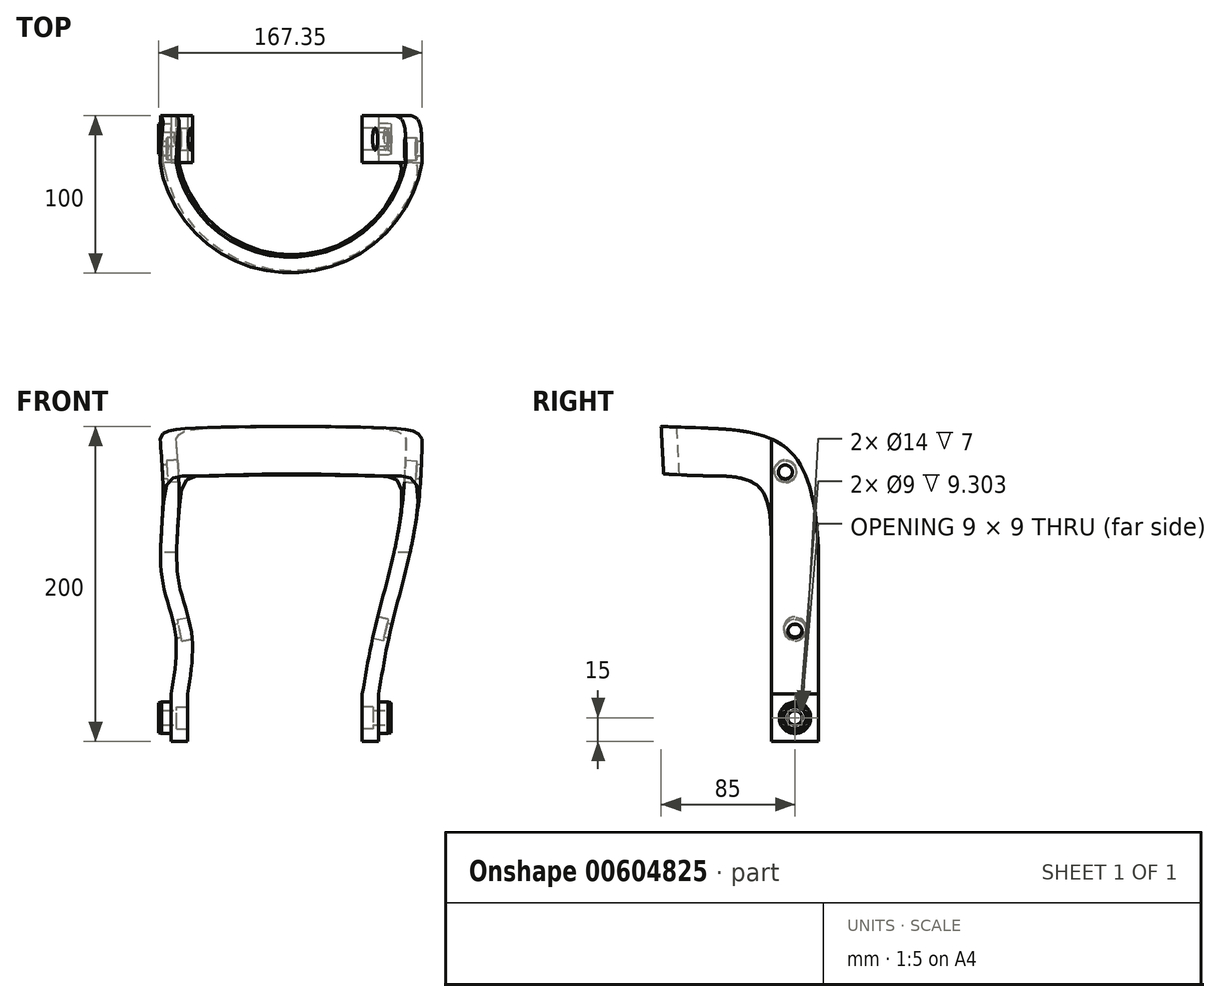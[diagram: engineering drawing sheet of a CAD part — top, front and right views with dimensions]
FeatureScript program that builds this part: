
annotation { "Feature Type Name" : "Feature", "Feature Type Description" : "" }
export const myFeature = defineFeature(function(context is Context, id is Id, definition is map)
    precondition{}
    {
        {
            var Q0;
            Q0=qCreatedBy(makeId("Top.planeOp"),FACE);
            var sketch = newSketch(context, id + "F0", { "sketchPlane" : qUnion([Q0])});
            skLineSegment(sketch, "E0", {"start": v(-55.5, 15) * mm, "end": v(-55.5, -15) * mm});
            skLineSegment(sketch, "E1", {"start": v(55.5, 15) * mm, "end": v(55.5, -15) * mm});
            skPoint(sketch, "E2", {"position": v(-55.5, 0) * mm});
            skPoint(sketch, "E3", {"position": v(55.5, 0) * mm});
            skLineSegment(sketch, "E4", {"start": v(-55.5, 15) * mm, "end": v(-65.81, 15) * mm});
            skLineSegment(sketch, "E5", {"start": v(-65.81, 15) * mm, "end": v(-65.81, -15) * mm});
            skLineSegment(sketch, "E6", {"start": v(55.5, 15) * mm, "end": v(65.81, 15) * mm});
            skLineSegment(sketch, "E7", {"start": v(65.81, 15) * mm, "end": v(65.81, -15) * mm});
            skLineSegment(sketch, "E8", {"start": v(-65.81, -15) * mm, "end": v(-55.5, -15) * mm});
            skLineSegment(sketch, "E9", {"start": v(55.5, -15) * mm, "end": v(65.81, -15) * mm});
            skSolve(sketch);
        }
        {
            var Q0;
            Q0=qCreatedBy(makeId("Top.planeOp"),FACE);
            cPlane(context, id + "F1", {"entities" : qUnion([Q0]), "cplaneType" : CPlaneType.OFFSET, "offset" : 30 * mm, "width" : 150 * mm, "height" : 150 * mm});
        }
        {
            var Q0;
            Q0=qCreatedBy(id+"F1.planeOp",FACE);
            var sketch = newSketch(context, id + "F2", { "sketchPlane" : qUnion([Q0])});
            skArc(sketch, "E10", {"start": v(-55.5, -15) * mm, "mid": v(0, -57.5) * mm, "end": v(55.5, -15) * mm});
            skArc(sketch, "E11", {"start": v(-65.81, -15) * mm, "mid": v(0, -67.5) * mm, "end": v(65.81, -15) * mm});
            skLineSegment(sketch, "E12", {"start": v(-55.5, 15) * mm, "end": v(-55.5, -15) * mm});
            skLineSegment(sketch, "E13", {"start": v(55.5, 15) * mm, "end": v(55.5, -15) * mm});
            skPoint(sketch, "E14", {"position": v(-55.5, 0) * mm});
            skPoint(sketch, "E15", {"position": v(55.5, 0) * mm});
            skLineSegment(sketch, "E16", {"start": v(-55.5, 15) * mm, "end": v(-65.81, 15) * mm});
            skLineSegment(sketch, "E17", {"start": v(-65.81, 15) * mm, "end": v(-65.81, -15) * mm});
            skLineSegment(sketch, "E18", {"start": v(55.5, 15) * mm, "end": v(65.81, 15) * mm});
            skLineSegment(sketch, "E19", {"start": v(65.81, 15) * mm, "end": v(65.81, -15) * mm});
            skSolve(sketch);
        }
        {
            var Q0;
            Q0=qCreatedBy(makeId("Top.planeOp"),FACE);
            cPlane(context, id + "F3", {"entities" : qUnion([Q0]), "cplaneType" : CPlaneType.OFFSET, "offset" : 70 * mm, "width" : 150 * mm, "height" : 150 * mm});
        }
        {
            var Q0;
            Q0=qCreatedBy(id+"F3.planeOp",FACE);
            var sketch = newSketch(context, id + "F4", { "sketchPlane" : qUnion([Q0])});
            skPoint(sketch, "E20", {"position": v(5, 0) * mm});
            skPoint(sketch, "E21.center.orphan", {"position": v(0, 0) * mm});
            skArc(sketch, "E22", {"start": v(-53.1, -15) * mm, "mid": v(5, -60) * mm, "end": v(63.1, -15) * mm});
            skArc(sketch, "E23", {"start": v(-63.37, -15) * mm, "mid": v(5, -70) * mm, "end": v(73.37, -15) * mm});
            skLineSegment(sketch, "E24", {"start": v(-53.1, 15) * mm, "end": v(-53.1, -15) * mm});
            skLineSegment(sketch, "E25", {"start": v(63.1, 15) * mm, "end": v(63.1, -15) * mm});
            skPoint(sketch, "E26", {"position": v(-53.1, 0) * mm});
            skLineSegment(sketch, "E27", {"start": v(-53.1, 15) * mm, "end": v(-63.37, 15) * mm});
            skLineSegment(sketch, "E28", {"start": v(-63.37, 15) * mm, "end": v(-63.37, -15) * mm});
            skLineSegment(sketch, "E29", {"start": v(63.1, 15) * mm, "end": v(73.37, 15) * mm});
            skLineSegment(sketch, "E30", {"start": v(73.37, 15) * mm, "end": v(73.37, -15) * mm});
            skSolve(sketch);
        }
        {
            var Q0;
            Q0=qCreatedBy(makeId("Top.planeOp"),FACE);
            cPlane(context, id + "F5", {"entities" : qUnion([Q0]), "cplaneType" : CPlaneType.OFFSET, "offset" : 100 * mm, "width" : 150 * mm, "height" : 150 * mm});
        }
        {
            var Q0;
            Q0=qCreatedBy(id+"F5.planeOp",FACE);
            var sketch = newSketch(context, id + "F6", { "sketchPlane" : qUnion([Q0])});
            skPoint(sketch, "E31", {"position": v(5, 0) * mm});
            skArc(sketch, "E32", {"start": v(-60.81, -15) * mm, "mid": v(5, -67.5) * mm, "end": v(70.81, -15) * mm});
            skArc(sketch, "E33", {"start": v(-71.03, -15) * mm, "mid": v(5, -77.5) * mm, "end": v(81.03, -15) * mm});
            skLineSegment(sketch, "E34", {"start": v(-60.81, 15) * mm, "end": v(-60.81, -15) * mm});
            skLineSegment(sketch, "E35", {"start": v(70.81, 15) * mm, "end": v(70.81, -15) * mm});
            skLineSegment(sketch, "E36", {"start": v(-60.81, 15) * mm, "end": v(-71.03, 15) * mm});
            skLineSegment(sketch, "E37", {"start": v(-71.03, 15) * mm, "end": v(-71.03, -15) * mm});
            skLineSegment(sketch, "E38", {"start": v(70.81, 15) * mm, "end": v(81.03, 15) * mm});
            skLineSegment(sketch, "E39", {"start": v(81.03, 15) * mm, "end": v(81.03, -15) * mm});
            skSolve(sketch);
        }
        {
            var Q0;
            Q0=qCreatedBy(makeId("Top.planeOp"),FACE);
            cPlane(context, id + "F7", {"entities" : qUnion([Q0]), "cplaneType" : CPlaneType.OFFSET, "offset" : 150 * mm, "width" : 150 * mm, "height" : 150 * mm});
        }
        {
            var Q0;
            Q0=qCreatedBy(id+"F7.planeOp",FACE);
            var sketch = newSketch(context, id + "F8", { "sketchPlane" : qUnion([Q0])});
            skPoint(sketch, "E40", {"position": v(10, 0) * mm});
            skArc(sketch, "E41", {"start": v(-60.93, -15) * mm, "mid": v(10, -72.5) * mm, "end": v(80.93, -15) * mm});
            skArc(sketch, "E42", {"start": v(-71.12, -15) * mm, "mid": v(10, -82.5) * mm, "end": v(91.12, -15) * mm});
            skLineSegment(sketch, "E43", {"start": v(-60.93, 15) * mm, "end": v(-60.93, -15) * mm});
            skLineSegment(sketch, "E44", {"start": v(80.93, -15) * mm, "end": v(80.93, 15) * mm});
            skPoint(sketch, "E45", {"position": v(-60.93, 0) * mm});
            skPoint(sketch, "E46", {"position": v(80.93, 0) * mm});
            skLineSegment(sketch, "E47", {"start": v(-60.93, 15) * mm, "end": v(-71.12, 15) * mm});
            skLineSegment(sketch, "E48", {"start": v(-71.12, 15) * mm, "end": v(-71.12, -15) * mm});
            skLineSegment(sketch, "E49", {"start": v(80.93, 15) * mm, "end": v(91.12, 15) * mm});
            skLineSegment(sketch, "E50", {"start": v(91.12, 15) * mm, "end": v(91.12, -15) * mm});
            skSolve(sketch);
        }
        {
            var Q0;
            Q0=qCreatedBy(makeId("Top.planeOp"),FACE);
            cPlane(context, id + "F9", {"entities" : qUnion([Q0]), "cplaneType" : CPlaneType.OFFSET, "offset" : 200 * mm, "width" : 150 * mm, "height" : 150 * mm});
        }
        {
            var Q0;
            Q0=qCreatedBy(id+"F9.planeOp",FACE);
            var sketch = newSketch(context, id + "F10", { "sketchPlane" : qUnion([Q0])});
            skPoint(sketch, "E51", {"position": v(10, 0) * mm});
            skArc(sketch, "E52", {"start": v(-63.48, -15) * mm, "mid": v(10, -75) * mm, "end": v(83.48, -15) * mm});
            skArc(sketch, "E53", {"start": v(-73.67, -15) * mm, "mid": v(10, -85) * mm, "end": v(93.67, -15) * mm});
            skLineSegment(sketch, "E54", {"start": v(-63.48, 15) * mm, "end": v(-63.48, -15) * mm});
            skLineSegment(sketch, "E55", {"start": v(83.48, 15) * mm, "end": v(83.48, -15) * mm});
            skLineSegment(sketch, "E56", {"start": v(-63.48, 15) * mm, "end": v(-73.67, 15) * mm});
            skLineSegment(sketch, "E57", {"start": v(-73.67, 15) * mm, "end": v(-73.67, -15) * mm});
            skLineSegment(sketch, "E58", {"start": v(83.48, 15) * mm, "end": v(93.67, 15) * mm});
            skLineSegment(sketch, "E59", {"start": v(93.67, 15) * mm, "end": v(93.67, -15) * mm});
            skSolve(sketch);
        }
        {
            var Q0;
            Q0=qSketchRegion(id+"F2",true);
            var Q1;
            Q1=qSketchRegion(id+"F4",true);
            var Q2;
            Q2=qSketchRegion(id+"F6",true);
            var Q3;
            Q3=qSketchRegion(id+"F8",true);
            var Q4;
            Q4=qSketchRegion(id+"F10",true);
            loft(context, id + "F11", {"sheetProfilesArray" : [{ "sheetProfileEntities" : qUnion([Q0]) }, { "sheetProfileEntities" : qUnion([Q1]) }, { "sheetProfileEntities" : qUnion([Q2]) }, { "sheetProfileEntities" : qUnion([Q3]) }, { "sheetProfileEntities" : qUnion([Q4]) }]});
        }
        {
            var Q0;
            Q0=qCreatedBy(makeId("Right.planeOp"),FACE);
            cPlane(context, id + "F12", {"entities" : qUnion([Q0]), "cplaneType" : CPlaneType.OFFSET, "offset" : 77 * mm, "oppositeDirection" : true, "width" : 150 * mm, "height" : 150 * mm});
        }
        {
            var Q0;
            Q0=qCreatedBy(id+"F12.planeOp",FACE);
            var sketch = newSketch(context, id + "F13", { "sketchPlane" : qUnion([Q0])});
            skPoint(sketch, "E60", {"position": v(-85, 200) * mm});
            skLineSegment(sketch, "E61", {"start": v(-85, 200) * mm, "end": v(-85, 170) * mm});
            skPoint(sketch, "E62", {"position": v(15, 200) * mm});
            skLineSegment(sketch, "E63", {"start": v(15, 200) * mm, "end": v(15, 120) * mm});
            skPoint(sketch, "E64", {"position": v(15, 0) * mm});
            skPoint(sketch, "E65", {"position": v(-15, 0) * mm});
            skPoint(sketch, "E66", {"position": v(-15, 200) * mm});
            skFitSpline(sketch, "E67", {"points": [v(-85, 200) * mm, v(15, 120) * mm], "startDerivative": vector(199.24, -8.69) * mm, "endDerivative": vector(9.95, -251.27) * mm});
            skPoint(sketch, "E68", {"position": v(-56.51, 168.7) * mm});
            skPoint(sketch, "E69", {"position": v(-23.21, 161.98) * mm});
            skPoint(sketch, "E70", {"position": v(-50.86, 198.7) * mm});
            skPoint(sketch, "E71", {"position": v(-4.39, 185.34) * mm});
            skPoint(sketch, "E72", {"position": v(-15, 120) * mm});
            skFitSpline(sketch, "E73", {"points": [v(-15, 120) * mm, v(-23.21, 161.98) * mm, v(-56.51, 168.7) * mm, v(-85, 170) * mm], "startDerivative": vector(0.5, 138.75) * mm, "endDerivative": vector(-88.02, 5.85) * mm});
            skLineSegment(sketch, "E74", {"start": v(-15, 120) * mm, "end": v(-15, 0) * mm});
            skLineSegment(sketch, "E75", {"start": v(15, 0) * mm, "end": v(15, 120) * mm});
            skLineSegment(sketch, "E76", {"start": v(-85, 200) * mm, "end": v(15, 200) * mm});
            skLineSegment(sketch, "E77", {"start": v(-85, 170) * mm, "end": v(-82.46, 0) * mm});
            skLineSegment(sketch, "E78", {"start": v(-82.46, 0) * mm, "end": v(-15, 0) * mm});
            skLineSegment(sketch, "E79", {"start": v(-85, 170) * mm, "end": v(-85, 200) * mm});
            skSolve(sketch);
        }
        {
            var Q0;
            Q0=qSketchRegion(id+"F13",true);
            extrude(context, id + "F14", {"entities" : qUnion([Q0]), "operationType" : NewBodyOperationType.REMOVE, "depth" : 300 * mm, "offsetDistance" : 25 * mm});
        }
        {
            var Q0;
            Q0=qCreatedBy(id+"F12.planeOp",FACE);
            var sketch = newSketch(context, id + "F15", { "sketchPlane" : qUnion([Q0])});
            skPoint(sketch, "E80", {"position": v(-8.62, 171.05) * mm});
            skLineSegment(sketch, "E81.bottom", {"start": v(-11.12, 161.05) * mm, "end": v(-6.12, 161.05) * mm});
            skLineSegment(sketch, "E81.top", {"start": v(-11.12, 181.05) * mm, "end": v(-6.12, 181.05) * mm});
            skLineSegment(sketch, "E81.left", {"start": v(-11.12, 161.05) * mm, "end": v(-11.12, 181.05) * mm});
            skLineSegment(sketch, "E81.right", {"start": v(-6.12, 161.05) * mm, "end": v(-6.12, 181.05) * mm});
            skSolve(sketch);
        }
        {
            var Q0;
            Q0=qSketchRegion(id+"F0",true);
            extrude(context, id + "F16", {"entities" : qUnion([Q0]), "operationType" : NewBodyOperationType.ADD, "depth" : 30 * mm, "offsetDistance" : 25 * mm});
        }
        {
            var Q0;
            Q0=makeQuery(id+"F16.opExtrude","SWEPT_FACE",FACE,{"disambiguationData":[OSD([sQuery(id+"F0.wireOp",EDGE,"E7")])]});
            var sketch = newSketch(context, id + "F17", { "sketchPlane" : qUnion([Q0])});
            skPoint(sketch, "E82", {"position": v(-15, 30) * mm});
            skPoint(sketch, "E83", {"position": v(-15, 0) * mm});
            skPoint(sketch, "E84", {"position": v(0, 15) * mm});
            skCircle(sketch, "E85", {"center": v(0, 15) * mm, "radius": 10 * mm});
            skSolve(sketch);
        }
        {
            var Q0;
            Q0=qSketchRegion(id+"F17",true);
            extrude(context, id + "F18", {"entities" : qUnion([Q0]), "operationType" : NewBodyOperationType.ADD, "depth" : 6 * mm, "offsetDistance" : 25 * mm});
        }
        {
            var Q0;
            Q0=makeQuery(id+"F18.opExtrude","CAP_FACE",FACE,{"disambiguationData":[OSD([sQuery(id+"F17.wireOp",EDGE,"E85")])],"isStart":false});
            cPlane(context, id + "F19", {"entities" : qUnion([Q0]), "cplaneType" : CPlaneType.OFFSET, "offset" : 0 * mm, "width" : 150 * mm, "height" : 150 * mm});
        }
        {
            var Q0;
            Q0=makeQuery(id+"F16.opExtrude","SWEPT_FACE",FACE,{"disambiguationData":[OSD([sQuery(id+"F0.wireOp",EDGE,"E1")])]});
            cPlane(context, id + "F20", {"entities" : qUnion([Q0]), "cplaneType" : CPlaneType.OFFSET, "offset" : 0 * mm, "width" : 150 * mm, "height" : 150 * mm});
        }
        {
            var Q0;
            Q0=qCreatedBy(id+"F20.planeOp",FACE);
            var sketch = newSketch(context, id + "F21", { "sketchPlane" : qUnion([Q0])});
            skPoint(sketch, "E86", {"position": v(0, 0) * mm});
            skPoint(sketch, "E87", {"position": v(0, 15) * mm});
            skCircle(sketch, "E88", {"center": v(0, 15) * mm, "radius": 7 * mm});
            skSolve(sketch);
        }
        {
            var Q0;
            Q0=qSketchRegion(id+"F21",true);
            extrude(context, id + "F22", {"entities" : qUnion([Q0]), "operationType" : NewBodyOperationType.REMOVE, "oppositeDirection" : true, "depth" : 7 * mm, "offsetDistance" : 25 * mm});
        }
        {
            var Q0;
            Q0=makeQuery(id+"F16.opExtrude","SWEPT_FACE",FACE,{"disambiguationData":[OSD([sQuery(id+"F0.wireOp",EDGE,"E5")])]});
            cPlane(context, id + "F23", {"entities" : qUnion([Q0]), "cplaneType" : CPlaneType.OFFSET, "offset" : 0 * mm, "width" : 150 * mm, "height" : 150 * mm});
        }
        {
            var Q0;
            Q0=qCreatedBy(id+"F23.planeOp",FACE);
            var sketch = newSketch(context, id + "F24", { "sketchPlane" : qUnion([Q0])});
            skPoint(sketch, "E89", {"position": v(0, 15) * mm});
            skCircle(sketch, "E90", {"center": v(0, 15) * mm, "radius": 10 * mm});
            skSolve(sketch);
        }
        {
            var Q0;
            Q0=qSketchRegion(id+"F24",true);
            extrude(context, id + "F25", {"entities" : qUnion([Q0]), "operationType" : NewBodyOperationType.ADD, "depth" : 6 * mm, "offsetDistance" : 25 * mm});
        }
        {
            var Q0;
            Q0=makeQuery(id+"F25.opExtrude","CAP_FACE",FACE,{"disambiguationData":[OSD([sQuery(id+"F24.wireOp",EDGE,"E90")])],"isStart":false});
            cPlane(context, id + "F26", {"entities" : qUnion([Q0]), "cplaneType" : CPlaneType.OFFSET, "offset" : 0 * mm, "width" : 150 * mm, "height" : 150 * mm});
        }
        {
            var Q0;
            Q0=makeQuery(id+"F16.opExtrude","SWEPT_FACE",FACE,{"disambiguationData":[OSD([sQuery(id+"F0.wireOp",EDGE,"E0")])]});
            cPlane(context, id + "F27", {"entities" : qUnion([Q0]), "cplaneType" : CPlaneType.OFFSET, "offset" : 0 * mm, "width" : 150 * mm, "height" : 150 * mm});
        }
        {
            var Q0;
            Q0=qCreatedBy(id+"F27.planeOp",FACE);
            var sketch = newSketch(context, id + "F28", { "sketchPlane" : qUnion([Q0])});
            skPoint(sketch, "E91", {"position": v(0, 0) * mm});
            skPoint(sketch, "E92", {"position": v(0, 15) * mm});
            skCircle(sketch, "E93", {"center": v(0, 15) * mm, "radius": 7 * mm});
            skSolve(sketch);
        }
        {
            var Q0;
            Q0=qSketchRegion(id+"F28",true);
            extrude(context, id + "F29", {"entities" : qUnion([Q0]), "operationType" : NewBodyOperationType.REMOVE, "oppositeDirection" : true, "depth" : 7 * mm, "offsetDistance" : 25 * mm});
        }
        {
            var Q0;
            Q0=makeQuery(id+"F16.opExtrude","CAP_FACE",FACE,{"disambiguationData":[OSD([sQuery(id+"F0.wireOp",EDGE,"E1"),sQuery(id+"F0.wireOp",EDGE,"E6"),sQuery(id+"F0.wireOp",EDGE,"E7"),sQuery(id+"F0.wireOp",EDGE,"E9")])],"isStart":true});
            cPlane(context, id + "F30", {"entities" : qUnion([Q0]), "cplaneType" : CPlaneType.OFFSET, "offset" : 15 * mm, "oppositeDirection" : true, "width" : 150 * mm, "height" : 150 * mm});
        }
        {
            var Q0;
            Q0=qCreatedBy(id+"F30.planeOp",FACE);
            var sketch = newSketch(context, id + "F31", { "sketchPlane" : qUnion([Q0])});
            skPoint(sketch, "E94", {"position": v(60.66, -15) * mm});
            skLineSegment(sketch, "E95", {"start": v(60.66, -15) * mm, "end": v(61.72, -15) * mm, "construction": true});
            skPoint(sketch, "E96", {"position": v(71.81, 4.05) * mm});
            skPoint(sketch, "E97", {"position": v(71.81, -12) * mm});
            skPoint(sketch, "E98", {"position": v(71.81, -15) * mm});
            skPoint(sketch, "E99", {"position": v(41.37, 7.31) * mm});
            skPoint(sketch, "E100", {"position": v(71.81, -13.5) * mm});
            skPoint(sketch, "E101", {"position": v(73.81, -13.5) * mm});
            skPoint(sketch, "E102", {"position": v(73.81, -12.5) * mm});
            skPoint(sketch, "E103", {"position": v(73.81, -14.5) * mm});
            skLineSegment(sketch, "E104", {"start": v(71.81, -12) * mm, "end": v(71.81, -15) * mm});
            skPoint(sketch, "E105", {"position": v(71.81, 0) * mm});
            skPoint(sketch, "E106", {"position": v(71.81, -10) * mm});
            skPoint(sketch, "E107", {"position": v(65.81, -10) * mm});
            skPoint(sketch, "E108", {"position": v(65.81, -7) * mm});
            skPoint(sketch, "E109", {"position": v(65.81, -8.5) * mm});
            skPoint(sketch, "E110", {"position": v(67.81, -8.5) * mm});
            skPoint(sketch, "E111", {"position": v(67.81, -7.5) * mm});
            skPoint(sketch, "E112", {"position": v(67.81, -9.5) * mm});
            skPoint(sketch, "E113", {"position": v(65.81, 0) * mm});
            skLineSegment(sketch, "E114.trimOffspring", {"start": v(71.81, -10) * mm, "end": v(71.81, -16.41) * mm, "construction": true});
            skPoint(sketch, "E115", {"position": v(71.81, -7) * mm});
            skPoint(sketch, "E116", {"position": v(71.81, -8.5) * mm});
            skPoint(sketch, "E117", {"position": v(73.81, -8.5) * mm});
            skPoint(sketch, "E118", {"position": v(73.81, -7.5) * mm});
            skPoint(sketch, "E119", {"position": v(73.81, -9.5) * mm});
            skLineSegment(sketch, "E120", {"start": v(73.81, -7.5) * mm, "end": v(71.81, -7) * mm});
            skLineSegment(sketch, "E121", {"start": v(73.81, -9.5) * mm, "end": v(73.81, -7.5) * mm});
            skLineSegment(sketch, "E122", {"start": v(73.81, -9.5) * mm, "end": v(71.81, -10) * mm});
            skLineSegment(sketch, "E123", {"start": v(71.81, -7) * mm, "end": v(71.81, -10) * mm});
            skLineSegment(sketch, "E124", {"start": v(71.81, 0) * mm, "end": v(73.81, 0) * mm});
            skLineSegment(sketch, "E125", {"start": v(73.81, -8.5) * mm, "end": v(73.81, -9.5) * mm});
            skSolve(sketch);
        }
        {
            var Q0;
            Q0=qSketchRegion(id+"F31",true);
            var Q1;
            Q1=sQuery(id+"F31.wireOp",EDGE,"E124");
            revolve(context, id + "F32", {"operationType" : NewBodyOperationType.ADD, "entities" : qUnion([Q0]), "axis" : qUnion([Q1]), "revolveType" : RevolveType.FULL});
        }
        {
            var Q0;
            Q0=qCreatedBy(id+"F19.planeOp",FACE);
            var sketch = newSketch(context, id + "F33", { "sketchPlane" : qUnion([Q0])});
            skPoint(sketch, "E126", {"position": v(0, 15) * mm});
            skPoint(sketch, "E127", {"position": v(0, 0) * mm});
            skCircle(sketch, "E128", {"center": v(0, 15) * mm, "radius": 4.5 * mm});
            skSolve(sketch);
        }
        {
            var Q0;
            Q0=qSketchRegion(id+"F33",true);
            extrude(context, id + "F34", {"entities" : qUnion([Q0]), "operationType" : NewBodyOperationType.REMOVE, "oppositeDirection" : true, "depth" : 25 * mm, "offsetDistance" : 25 * mm});
        }
        {
            var Q0;
            Q0=makeQuery(id+"F16.opExtrude","CAP_FACE",FACE,{"disambiguationData":[OSD([sQuery(id+"F0.wireOp",EDGE,"E0"),sQuery(id+"F0.wireOp",EDGE,"E4"),sQuery(id+"F0.wireOp",EDGE,"E5"),sQuery(id+"F0.wireOp",EDGE,"E8")])],"isStart":true});
            cPlane(context, id + "F35", {"entities" : qUnion([Q0]), "cplaneType" : CPlaneType.OFFSET, "offset" : 15 * mm, "oppositeDirection" : true, "width" : 150 * mm, "height" : 150 * mm});
        }
        {
            var Q0;
            Q0=qCreatedBy(id+"F35.planeOp",FACE);
            var sketch = newSketch(context, id + "F36", { "sketchPlane" : qUnion([Q0])});
            skPoint(sketch, "E129", {"position": v(-60.91, -32.93) * mm});
            skPoint(sketch, "E130", {"position": v(-65.81, -10) * mm});
            skPoint(sketch, "E131", {"position": v(-57.6, -34.18) * mm});
            skPoint(sketch, "E132", {"position": v(-65.81, -15) * mm});
            skPoint(sketch, "E133", {"position": v(-71.81, -10) * mm});
            skPoint(sketch, "E134", {"position": v(-71.81, -7) * mm});
            skPoint(sketch, "E135", {"position": v(-71.81, -8.5) * mm});
            skPoint(sketch, "E136", {"position": v(-73.81, -8.5) * mm});
            skPoint(sketch, "E137", {"position": v(-73.81, -9.5) * mm});
            skPoint(sketch, "E138", {"position": v(-73.81, -7.5) * mm});
            skLineSegment(sketch, "E139", {"start": v(-73.81, -9.5) * mm, "end": v(-71.81, -10) * mm});
            skLineSegment(sketch, "E140", {"start": v(-73.81, -7.5) * mm, "end": v(-73.81, -9.5) * mm});
            skLineSegment(sketch, "E141", {"start": v(-73.81, -7.5) * mm, "end": v(-71.81, -7) * mm});
            skLineSegment(sketch, "E142", {"start": v(-71.81, -10) * mm, "end": v(-71.81, -7) * mm});
            skLineSegment(sketch, "E143", {"start": v(-73.81, -8.5) * mm, "end": v(-73.81, -7.5) * mm});
            skSolve(sketch);
        }
        {
            var Q0;
            Q0=qCreatedBy(id+"F35.planeOp",FACE);
            var sketch = newSketch(context, id + "F37", { "sketchPlane" : qUnion([Q0])});
            skPoint(sketch, "E144", {"position": v(-71.81, -10) * mm});
            skPoint(sketch, "E145", {"position": v(-71.81, 0) * mm});
            skLineSegment(sketch, "E146", {"start": v(-71.81, 0) * mm, "end": v(-73.81, 0) * mm});
            skSolve(sketch);
        }
        {
            var Q0;
            Q0=qSketchRegion(id+"F36",true);
            var Q1;
            Q1=sQuery(id+"F37.wireOp",EDGE,"E146");
            revolve(context, id + "F38", {"operationType" : NewBodyOperationType.ADD, "entities" : qUnion([Q0]), "axis" : qUnion([Q1]), "revolveType" : RevolveType.FULL});
        }
        {
            var Q0;
            Q0=qCreatedBy(id+"F27.planeOp",FACE);
            var sketch = newSketch(context, id + "F39", { "sketchPlane" : qUnion([Q0])});
            skPoint(sketch, "E147", {"position": v(0, 0) * mm});
            skPoint(sketch, "E148", {"position": v(0, 15) * mm});
            skCircle(sketch, "E149", {"center": v(0, 15) * mm, "radius": 4.5 * mm});
            skSolve(sketch);
        }
        {
            var Q0;
            Q0=qSketchRegion(id+"F39",true);
            extrude(context, id + "F40", {"entities" : qUnion([Q0]), "operationType" : NewBodyOperationType.REMOVE, "oppositeDirection" : true, "depth" : 25 * mm, "offsetDistance" : 25 * mm});
        }
        {
            var Q0;
            Q0=qCreatedBy(makeId("Front.planeOp"),FACE);
            var sketch = newSketch(context, id + "F41", { "sketchPlane" : qUnion([Q0])});
            skPoint(sketch, "E150", {"position": v(73.37, 70) * mm});
            skLineSegment(sketch, "E151", {"start": v(73.37, 70) * mm, "end": v(63.46, 72.38) * mm});
            skPoint(sketch, "E152", {"position": v(75.25, 77.79) * mm});
            skLineSegment(sketch, "E153", {"start": v(75.25, 77.79) * mm, "end": v(73.37, 70) * mm});
            skLineSegment(sketch, "E154", {"start": v(73.37, 70) * mm, "end": v(61.05, 70) * mm});
            skLineSegment(sketch, "E155", {"start": v(75.25, 77.79) * mm, "end": v(75.25, 67.22) * mm});
            skLineSegment(sketch, "E156", {"start": v(73.37, 70) * mm, "end": v(84.33, 70) * mm});
            skPoint(sketch, "E157", {"position": v(0, 86.32) * mm});
            skPoint(sketch, "E158", {"position": v(0, 70) * mm});
            skLineSegment(sketch, "E159", {"start": v(73.37, 70) * mm, "end": v(73.37, 43.45) * mm});
            skLineSegment(sketch, "E160", {"start": v(73.37, 43.45) * mm, "end": v(73.37, 82.09) * mm});
            skSolve(sketch);
        }
        {
            var Q0;
            Q0=qCreatedBy(makeId("Right.planeOp"),FACE);
            cPlane(context, id + "F42", {"entities" : qUnion([Q0]), "cplaneType" : CPlaneType.OFFSET, "offset" : 73.37 * mm, "width" : 150 * mm, "height" : 150 * mm});
        }
        {
            var Q0;
            Q0=qCreatedBy(id+"F42.planeOp",FACE);
            var sketch = newSketch(context, id + "F43", { "sketchPlane" : qUnion([Q0])});
            skPoint(sketch, "E161", {"position": v(0, 70) * mm});
            skLineSegment(sketch, "E162", {"start": v(0, 70) * mm, "end": v(42.97, 70) * mm});
            skLineSegment(sketch, "E163", {"start": v(42.97, 70) * mm, "end": v(-53.34, 70) * mm});
            skSolve(sketch);
        }
        {
            var Q0;
            Q0=sQuery(id+"F43.wireOp",EDGE,"E163");
            var Q1;
            Q1=qCreatedBy(id+"F3.planeOp",FACE);
            cPlane(context, id + "F44", {"entities" : qUnion([Q0, Q1]), "cplaneType" : CPlaneType.LINE_ANGLE, "offset" : 25 * mm, "angle" : 103.53 * degree, "oppositeDirection" : true, "width" : 150 * mm, "height" : 150 * mm});
        }
        {
            var Q0;
            Q0=qCreatedBy(id+"F44.planeOp",FACE);
            var sketch = newSketch(context, id + "F45", { "sketchPlane" : qUnion([Q0])});
            skPoint(sketch, "E164", {"position": v(-7.5, 50.04) * mm});
            skPoint(sketch, "E165", {"position": v(0, 85.22) * mm});
            skCircle(sketch, "E166", {"center": v(0, 85.22) * mm, "radius": 4.5 * mm});
            skSolve(sketch);
        }
        {
            var Q0;
            Q0 = qSketchRegion(id + "F45", true);
            extrude(context, id + "F46", {"entities" : qUnion([Q0]), "operationType" : NewBodyOperationType.REMOVE, "depth" : 50 * mm, "offsetDistance" : 25 * mm});
        }
        {
            var Q0;
            Q0 = qSketchRegion(id + "F45", true);
            extrude(context, id + "F47", {"entities" : qUnion([Q0]), "operationType" : NewBodyOperationType.REMOVE, "oppositeDirection" : true, "depth" : 25 * mm, "offsetDistance" : 25 * mm});
        }
        {
            var Q0;
            Q0=qCreatedBy(id+"F44.planeOp",FACE);
            cPlane(context, id + "F48", {"entities" : qUnion([Q0]), "cplaneType" : CPlaneType.OFFSET, "offset" : 10 * mm, "width" : 150 * mm, "height" : 150 * mm});
        }
        {
            var Q0;
            Q0=qCreatedBy(id+"F48.planeOp",FACE);
            var sketch = newSketch(context, id + "F49", { "sketchPlane" : qUnion([Q0])});
            skPoint(sketch, "E167", {"position": v(0, 85.22) * mm});
            skCircle(sketch, "E168", {"center": v(0, 85.22) * mm, "radius": 7 * mm});
            skSolve(sketch);
        }
        {
            var Q0;
            Q0 = qSketchRegion(id + "F49", true);
            extrude(context, id + "F50", {"entities" : qUnion([Q0]), "operationType" : NewBodyOperationType.REMOVE, "oppositeDirection" : true, "depth" : 7 * mm, "offsetDistance" : 25 * mm});
        }
        {
            var Q0;
            Q0 = qSketchRegion(id + "F49", true);
            extrude(context, id + "F51", {"entities" : qUnion([Q0]), "operationType" : NewBodyOperationType.REMOVE, "depth" : 25 * mm, "offsetDistance" : 25 * mm});
        }
        {
            var Q0;
            Q0=qCreatedBy(makeId("Front.planeOp"),FACE);
            var sketch = newSketch(context, id + "F52", { "sketchPlane" : qUnion([Q0])});
            skPoint(sketch, "E169", {"position": v(-63.37, 70) * mm});
            skLineSegment(sketch, "E170", {"start": v(-63.37, 70) * mm, "end": v(-50.4, 70) * mm});
            skLineSegment(sketch, "E171", {"start": v(-50.4, 70) * mm, "end": v(-73.13, 70) * mm});
            skLineSegment(sketch, "E172", {"start": v(-63.37, 70) * mm, "end": v(-63.37, 75.73) * mm});
            skLineSegment(sketch, "E173", {"start": v(-63.37, 75.73) * mm, "end": v(-63.37, 61.67) * mm});
            skPoint(sketch, "E174", {"position": v(-64.51, 75.7) * mm});
            skLineSegment(sketch, "E175", {"start": v(-64.51, 75.7) * mm, "end": v(-63.37, 70) * mm});
            skSolve(sketch);
        }
        {
            var Q0;
            Q0=qCreatedBy(makeId("Right.planeOp"),FACE);
            cPlane(context, id + "F53", {"entities" : qUnion([Q0]), "cplaneType" : CPlaneType.OFFSET, "offset" : 63.37 * mm, "oppositeDirection" : true, "width" : 150 * mm, "height" : 150 * mm});
        }
        {
            var Q0;
            Q0=qCreatedBy(id+"F53.planeOp",FACE);
            var sketch = newSketch(context, id + "F54", { "sketchPlane" : qUnion([Q0])});
            skPoint(sketch, "E176", {"position": v(0, 70) * mm});
            skLineSegment(sketch, "E177", {"start": v(0, 70) * mm, "end": v(25.43, 70) * mm});
            skLineSegment(sketch, "E178", {"start": v(25.43, 70) * mm, "end": v(-27.36, 70) * mm});
            skSolve(sketch);
        }
        {
            var Q0;
            Q0=sQuery(id+"F54.wireOp",EDGE,"E178");
            var Q1;
            Q1=qCreatedBy(id+"F3.planeOp",FACE);
            cPlane(context, id + "F55", {"entities" : qUnion([Q0, Q1]), "cplaneType" : CPlaneType.LINE_ANGLE, "offset" : 25 * mm, "angle" : 101.3 * degree, "width" : 150 * mm, "height" : 150 * mm});
        }
        {
            var Q0;
            Q0=qCreatedBy(id+"F55.planeOp",FACE);
            var sketch = newSketch(context, id + "F56", { "sketchPlane" : qUnion([Q0])});
            skPoint(sketch, "E179", {"position": v(-3.92, 95.47) * mm});
            skPoint(sketch, "E180", {"position": v(0, 81.05) * mm});
            skCircle(sketch, "E181", {"center": v(0, 81.05) * mm, "radius": 4.5 * mm});
            skSolve(sketch);
        }
        {
            var Q0;
            Q0 = qSketchRegion(id + "F56", true);
            extrude(context, id + "F57", {"entities" : qUnion([Q0]), "operationType" : NewBodyOperationType.REMOVE, "oppositeDirection" : true, "depth" : 25 * mm, "offsetDistance" : 25 * mm});
        }
        {
            var Q0;
            Q0 = qSketchRegion(id + "F56", true);
            extrude(context, id + "F58", {"entities" : qUnion([Q0]), "operationType" : NewBodyOperationType.REMOVE, "depth" : 25 * mm, "offsetDistance" : 25 * mm});
        }
        {
            var Q0;
            Q0=qCreatedBy(id+"F55.planeOp",FACE);
            cPlane(context, id + "F59", {"entities" : qUnion([Q0]), "cplaneType" : CPlaneType.OFFSET, "offset" : 10 * mm, "width" : 150 * mm, "height" : 150 * mm});
        }
        {
            var Q0;
            Q0=qCreatedBy(id+"F59.planeOp",FACE);
            var sketch = newSketch(context, id + "F60", { "sketchPlane" : qUnion([Q0])});
            skPoint(sketch, "E182", {"position": v(0, 81.05) * mm});
            skCircle(sketch, "E183", {"center": v(0, 81.05) * mm, "radius": 7 * mm});
            skSolve(sketch);
        }
        {
            var Q0;
            Q0 = qSketchRegion(id + "F60", true);
            extrude(context, id + "F61", {"entities" : qUnion([Q0]), "operationType" : NewBodyOperationType.REMOVE, "oppositeDirection" : true, "depth" : 7 * mm, "offsetDistance" : 25 * mm});
        }
        {
            var Q0;
            Q0 = qSketchRegion(id + "F60", true);
            extrude(context, id + "F62", {"entities" : qUnion([Q0]), "operationType" : NewBodyOperationType.REMOVE, "depth" : 25 * mm, "offsetDistance" : 25 * mm});
        }
        {
            var Q0;
            Q0=qCreatedBy(makeId("Front.planeOp"),FACE);
            var sketch = newSketch(context, id + "F63", { "sketchPlane" : qUnion([Q0])});
            skPoint(sketch, "E184", {"position": v(-71.4, 171.06) * mm});
            skPoint(sketch, "E185", {"position": v(92.88, 171.04) * mm});
            skLineSegment(sketch, "E186", {"start": v(-71.4, 171.06) * mm, "end": v(-71.4, 188.4) * mm});
            skLineSegment(sketch, "E187", {"start": v(-71.4, 188.4) * mm, "end": v(-71.4, 150.8) * mm});
            skLineSegment(sketch, "E188", {"start": v(-71.4, 171.06) * mm, "end": v(-97.97, 171.06) * mm});
            skPoint(sketch, "E189", {"position": v(-72.56, 187.66) * mm});
            skLineSegment(sketch, "E190", {"start": v(-72.56, 187.66) * mm, "end": v(-71.4, 171.06) * mm});
            skSolve(sketch);
        }
        {
            var Q0;
            Q0=qCreatedBy(makeId("Right.planeOp"),FACE);
            cPlane(context, id + "F64", {"entities" : qUnion([Q0]), "cplaneType" : CPlaneType.OFFSET, "offset" : 92.88 * mm, "width" : 150 * mm, "height" : 150 * mm});
        }
        {
            var Q0;
            Q0=qCreatedBy(id+"F64.planeOp",FACE);
            var sketch = newSketch(context, id + "F65", { "sketchPlane" : qUnion([Q0])});
            skPoint(sketch, "E191", {"position": v(-6.12, 171.06) * mm});
            skLineSegment(sketch, "E192", {"start": v(-6.12, 171.06) * mm, "end": v(-23.57, 171.06) * mm});
            skLineSegment(sketch, "E193", {"start": v(-23.57, 171.06) * mm, "end": v(12.77, 171.06) * mm});
            skSolve(sketch);
        }
        {
            var Q0;
            Q0=qCreatedBy(makeId("Front.planeOp"),FACE);
            var sketch = newSketch(context, id + "F66", { "sketchPlane" : qUnion([Q0])});
            skPoint(sketch, "E194", {"position": v(92.88, 171.06) * mm});
            skPoint(sketch, "E195", {"position": v(0, 0) * mm});
            skSolve(sketch);
        }
        {
            var Q0;
            Q0=qCreatedBy(makeId("Top.planeOp"),FACE);
            cPlane(context, id + "F67", {"entities" : qUnion([Q0]), "cplaneType" : CPlaneType.OFFSET, "offset" : 171.06 * mm, "width" : 150 * mm, "height" : 150 * mm});
        }
        {
            var Q0;
            Q0=sQuery(id+"F65.wireOp",EDGE,"E193");
            var Q1;
            Q1=qCreatedBy(id+"F67.planeOp",FACE);
            cPlane(context, id + "F68", {"entities" : qUnion([Q0, Q1]), "cplaneType" : CPlaneType.LINE_ANGLE, "offset" : 25 * mm, "angle" : 86.15 * degree, "oppositeDirection" : true, "width" : 150 * mm, "height" : 150 * mm});
        }
        {
            var Q0;
            Q0=qCreatedBy(id+"F68.planeOp",FACE);
            var sketch = newSketch(context, id + "F69", { "sketchPlane" : qUnion([Q0])});
            skPoint(sketch, "E196", {"position": v(-6.12, 176.9) * mm});
            skCircle(sketch, "E197", {"center": v(-6.12, 176.9) * mm, "radius": 4.5 * mm});
            skSolve(sketch);
        }
        {
            var Q0;
            Q0 = qSketchRegion(id + "F69", true);
            extrude(context, id + "F70", {"entities" : qUnion([Q0]), "operationType" : NewBodyOperationType.REMOVE, "depth" : 25 * mm, "offsetDistance" : 25 * mm});
        }
        {
            var Q0;
            Q0 = qSketchRegion(id + "F69", true);
            extrude(context, id + "F71", {"entities" : qUnion([Q0]), "operationType" : NewBodyOperationType.REMOVE, "oppositeDirection" : true, "depth" : 25 * mm, "offsetDistance" : 25 * mm});
        }
        {
            var Q0;
            Q0=qCreatedBy(makeId("Right.planeOp"),FACE);
            cPlane(context, id + "F72", {"entities" : qUnion([Q0]), "cplaneType" : CPlaneType.OFFSET, "offset" : 71.4 * mm, "oppositeDirection" : true, "width" : 150 * mm, "height" : 150 * mm});
        }
        {
            var Q0;
            Q0=qCreatedBy(id+"F72.planeOp",FACE);
            var sketch = newSketch(context, id + "F73", { "sketchPlane" : qUnion([Q0])});
            skPoint(sketch, "E198", {"position": v(-240.56, 249.3) * mm});
            skPoint(sketch, "E199", {"position": v(-6.12, 171.06) * mm});
            skLineSegment(sketch, "E200", {"start": v(-6.12, 171.06) * mm, "end": v(-30.39, 171.06) * mm});
            skSolve(sketch);
        }
        {
            var Q0;
            Q0=sQuery(id+"F73.wireOp",EDGE,"E200");
            var Q1;
            Q1=qCreatedBy(id+"F67.planeOp",FACE);
            cPlane(context, id + "F74", {"entities" : qUnion([Q0, Q1]), "cplaneType" : CPlaneType.LINE_ANGLE, "offset" : 25 * mm, "angle" : 86.02 * degree, "oppositeDirection" : true, "width" : 150 * mm, "height" : 150 * mm});
        }
        {
            var Q0;
            Q0=qCreatedBy(id+"F74.planeOp",FACE);
            var sketch = newSketch(context, id + "F75", { "sketchPlane" : qUnion([Q0])});
            skPoint(sketch, "E201", {"position": v(6.12, 175.6) * mm});
            skCircle(sketch, "E202", {"center": v(6.12, 175.6) * mm, "radius": 4.5 * mm});
            skSolve(sketch);
        }
        {
            var Q0;
            Q0 = qSketchRegion(id + "F75", true);
            extrude(context, id + "F76", {"entities" : qUnion([Q0]), "operationType" : NewBodyOperationType.REMOVE, "oppositeDirection" : true, "depth" : 25 * mm, "offsetDistance" : 25 * mm});
        }
        {
            var Q0;
            Q0 = qSketchRegion(id + "F75", true);
            extrude(context, id + "F77", {"entities" : qUnion([Q0]), "operationType" : NewBodyOperationType.REMOVE, "depth" : 25 * mm, "offsetDistance" : 25 * mm});
        }
        {
            var Q0;
            Q0=qCreatedBy(id+"F74.planeOp",FACE);
            cPlane(context, id + "F78", {"entities" : qUnion([Q0]), "cplaneType" : CPlaneType.OFFSET, "offset" : 10 * mm, "oppositeDirection" : true, "width" : 150 * mm, "height" : 150 * mm});
        }
        {
            var Q0;
            Q0=qCreatedBy(id+"F78.planeOp",FACE);
            var sketch = newSketch(context, id + "F79", { "sketchPlane" : qUnion([Q0])});
            skPoint(sketch, "E203", {"position": v(6.12, 175.6) * mm});
            skCircle(sketch, "E204", {"center": v(6.12, 175.6) * mm, "radius": 7 * mm});
            skSolve(sketch);
        }
        {
            var Q0;
            Q0 = qSketchRegion(id + "F79", true);
            extrude(context, id + "F80", {"entities" : qUnion([Q0]), "operationType" : NewBodyOperationType.REMOVE, "oppositeDirection" : true, "depth" : 7 * mm, "offsetDistance" : 25 * mm});
        }
        {
            var Q0;
            Q0 = qSketchRegion(id + "F79", true);
            extrude(context, id + "F81", {"entities" : qUnion([Q0]), "operationType" : NewBodyOperationType.REMOVE, "depth" : 7 * mm, "offsetDistance" : 25 * mm});
        }
        {
            var Q0;
            Q0=qCreatedBy(id+"F68.planeOp",FACE);
            cPlane(context, id + "F82", {"entities" : qUnion([Q0]), "cplaneType" : CPlaneType.OFFSET, "offset" : 10 * mm, "oppositeDirection" : true, "width" : 150 * mm, "height" : 150 * mm});
        }
        {
            var Q0;
            Q0=qCreatedBy(id+"F82.planeOp",FACE);
            var sketch = newSketch(context, id + "F83", { "sketchPlane" : qUnion([Q0])});
            skPoint(sketch, "E205", {"position": v(-6.12, 176.9) * mm});
            skCircle(sketch, "E206", {"center": v(-6.12, 176.9) * mm, "radius": 7 * mm});
            skSolve(sketch);
        }
        {
            var Q0;
            Q0 = qSketchRegion(id + "F83", true);
            extrude(context, id + "F84", {"entities" : qUnion([Q0]), "operationType" : NewBodyOperationType.REMOVE, "oppositeDirection" : true, "depth" : 7 * mm, "offsetDistance" : 25 * mm});
        }
        {
            var Q0;
            Q0 = qSketchRegion(id + "F83", true);
            extrude(context, id + "F85", {"entities" : qUnion([Q0]), "operationType" : NewBodyOperationType.REMOVE, "depth" : 7 * mm, "offsetDistance" : 25 * mm});
        }
    });
